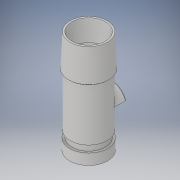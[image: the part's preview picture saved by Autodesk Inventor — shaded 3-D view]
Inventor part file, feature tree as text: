
AUTODESK INVENTOR PART (.ipt)
format: ipt  version: 2019.1 (Build 231200000, 200)  size: 409,600 bytes
history: native  units: mm
features: extrude x7, sketch x7, chamfer x2, other x1, fillet x1, plane x1, draft x1
ambient origin geometry x8: Origin, YZ Plane, XZ Plane, XY Plane, X Axis, Y Axis, Z Axis, Center Point
bodies: Solid1 (feature_tree)
feature tree (20):
  other  "CrossSection1"
  extrude  "Extrusion1"  Depth=35.0mm
  extrude  "Extrusion2"  Depth=10.0mm
  extrude  "Extrusion3"  Depth=50.0mm TaperAngle=0.0deg
  fillet  "Fillet1"  Radius=1.0mm
  plane  "Work Plane1"
  extrude  "Extrusion4"  Depth=10.0mm
  chamfer  "Chamfer1"  Distance=2.0mm
  extrude  "Extrusion5"  Depth=30.0mm
  extrude  "Extrusion6"  Depth=30.0mm
  chamfer  "Chamfer3"  Distance=10.0mm
  extrude  "Extrusion7"  Depth=30.0mm TaperAngle=0.0deg
  draft  "FaceDraft4"
  sketch  "Sketch1"  dims[d0=29.5mm d1=35.0mm]
  sketch  "Sketch2"  dims[d2=10.0mm d3=0.0mm d4=31.0mm]
  sketch  "Sketch3"  dims[d5=5.0mm d6=0.0mm d7=50.0mm d8=0.0mm d9=1.0mm]
  sketch  "Sketch4"  dims[d10=37.0mm d16=10.0mm]
  sketch  "Sketch5"  dims[d17=12.5mm]
  sketch  "Sketch6"  dims[d18=12.5mm]
  sketch  "Sketch9"  dims[d19=5.0mm d20=2.0mm d21=2.0mm d22=44.048322mm d23=10.0mm d24=0.0mm d25=4.0mm d26=0.0mm d27=1.5mm d28=2.0mm d29=45.0deg d30=1.5mm d31=0.0mm d32=37.0mm d33=30.0mm d34=0.0mm d38=0.5mm d39=2.0mm d40=45.0deg d44=0.5mm d45=2.0mm d46=-2.25mm d47=20.0mm d51=0.0mm d52=0.0mm d56=0.436332mm]
